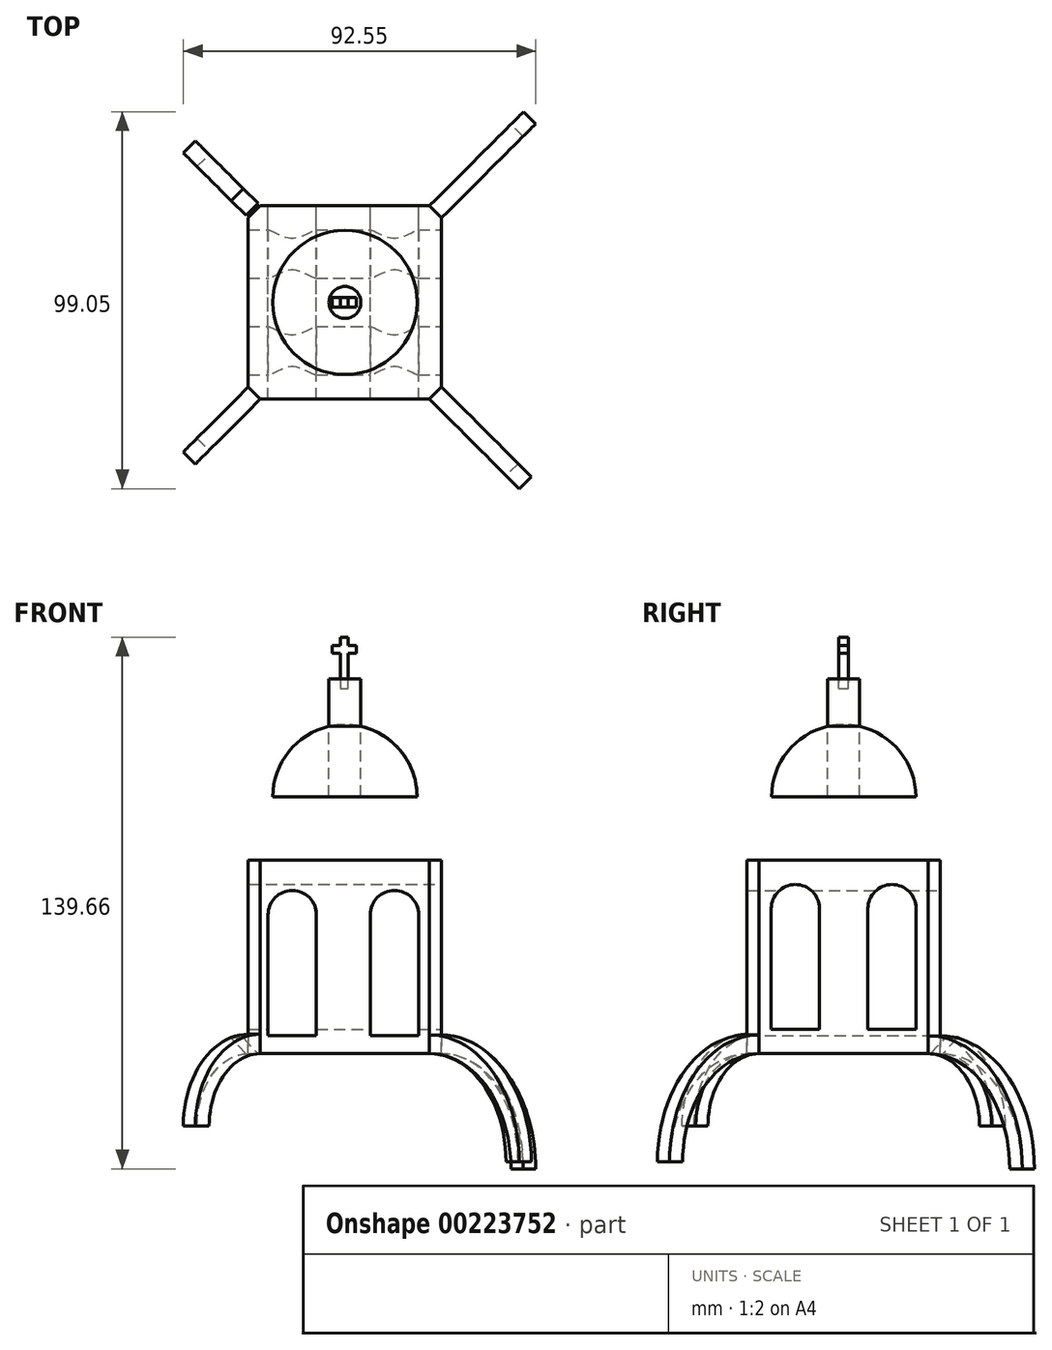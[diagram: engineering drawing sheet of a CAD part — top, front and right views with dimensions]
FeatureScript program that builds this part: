
annotation { "Feature Type Name" : "Feature", "Feature Type Description" : "" }
export const myFeature = defineFeature(function(context is Context, id is Id, definition is map)
    precondition{}
    {
        {
            var Q0;
            Q0=qCreatedBy(makeId("Front.planeOp"),FACE);
            var sketch = newSketch(context, id + "F0", { "sketchPlane" : qUnion([Q0])});
            skLineSegment(sketch, "E0.bottom", {"start": v(-25.4, -25.4) * mm, "end": v(25.4, -25.4) * mm});
            skLineSegment(sketch, "E0.top", {"start": v(-25.4, 25.4) * mm, "end": v(25.4, 25.4) * mm});
            skLineSegment(sketch, "E0.left", {"start": v(-25.4, -25.4) * mm, "end": v(-25.4, 25.4) * mm});
            skLineSegment(sketch, "E0.right", {"start": v(25.4, -25.4) * mm, "end": v(25.4, 25.4) * mm});
            skPoint(sketch, "E0.middle", {"position": v(0, 0) * mm});
            skLineSegment(sketch, "E1.bottom", {"start": v(0, 25.4) * mm, "end": v(-18.94, 25.4) * mm});
            skLineSegment(sketch, "E1.top", {"start": v(0, 42.12) * mm, "end": v(-18.94, 42.12) * mm});
            skLineSegment(sketch, "E1.left", {"start": v(0, 25.4) * mm, "end": v(0, 42.12) * mm});
            skLineSegment(sketch, "E1.right", {"start": v(-18.94, 25.4) * mm, "end": v(-18.94, 42.12) * mm});
            skArc(sketch, "E2", {"start": v(-18.94, 42.12) * mm, "mid": v(-13.4, 55.52) * mm, "end": v(0, 61.07) * mm});
            skLineSegment(sketch, "E3", {"start": v(0, 61.07) * mm, "end": v(0, 25.4) * mm});
            skLineSegment(sketch, "E4.bottom", {"start": v(0, 25.4) * mm, "end": v(-4.2, 25.4) * mm});
            skLineSegment(sketch, "E4.top", {"start": v(0, 73.03) * mm, "end": v(-4.2, 73.03) * mm});
            skLineSegment(sketch, "E4.left", {"start": v(0, 25.4) * mm, "end": v(0, 73.03) * mm});
            skLineSegment(sketch, "E4.right", {"start": v(-4.2, 25.4) * mm, "end": v(-4.2, 73.03) * mm});
            skSolve(sketch);
        }
        {
            var Q0;
            Q0=makeQuery(id+"F0.imprint","IMPRINT",FACE,{"disambiguationData":[TD([[makeQuery(id+"F0.imprint","IMPRINT",EDGE,{"derivedFrom":sQuery(id+"F0.wireOp",EDGE,"E0.bottom")}),1.0]])]});
            var sketch = newSketch(context, id + "F1", { "sketchPlane" : qUnion([Q0])});
            skLineSegment(sketch, "E5.bottom", {"start": v(-7.5, -20.63) * mm, "end": v(-20.2, -20.63) * mm});
            skLineSegment(sketch, "E5.top", {"start": v(-7.5, 11.12) * mm, "end": v(-20.2, 11.12) * mm});
            skLineSegment(sketch, "E5.left", {"start": v(-7.5, -20.63) * mm, "end": v(-7.5, 11.12) * mm});
            skLineSegment(sketch, "E5.right", {"start": v(-20.2, -20.63) * mm, "end": v(-20.2, 11.12) * mm});
            skPoint(sketch, "E5.middle", {"position": v(-13.84, -4.76) * mm});
            skLineSegment(sketch, "E6.bottom", {"start": v(6.65, -20.63) * mm, "end": v(19.35, -20.63) * mm});
            skLineSegment(sketch, "E6.top", {"start": v(6.65, 11.12) * mm, "end": v(19.35, 11.12) * mm});
            skLineSegment(sketch, "E6.left", {"start": v(6.65, -20.63) * mm, "end": v(6.65, 11.12) * mm});
            skLineSegment(sketch, "E6.right", {"start": v(19.35, -20.63) * mm, "end": v(19.35, 11.12) * mm});
            skPoint(sketch, "E6.middle", {"position": v(13, -4.76) * mm});
            skPoint(sketch, "E6.middle.positionSnap0", {"position": v(-7.5, -4.76) * mm});
            skPoint(sketch, "E6.centerSnap0", {"position": v(-7.5, -4.76) * mm});
            skArc(sketch, "E7", {"start": v(-7.5, 11.12) * mm, "mid": v(-13.84, 17.47) * mm, "end": v(-20.2, 11.12) * mm});
            skArc(sketch, "E8", {"start": v(19.35, 11.12) * mm, "mid": v(13, 17.47) * mm, "end": v(6.65, 11.12) * mm});
            skSolve(sketch);
        }
        {
            var Q0;
            {var subQ0=sQuery(id+"F0.wireOp",EDGE,"E1.top");Q0=makeQuery(id+"F0.imprint","IMPRINT",FACE,{"disambiguationData":[TD([[makeQuery(id+"F0.imprint","IMPRINT",EDGE,{"derivedFrom":subQ0}),-1.0]])]});}
            var Q1;
            {var subQ0=sQuery(id+"F0.wireOp",EDGE,"E1.bottom");Q1=makeQuery(id+"F0.imprint","IMPRINT",FACE,{"disambiguationData":[TD([[makeQuery(id+"F0.imprint","IMPRINT",EDGE,{"derivedFrom":subQ0}),-1.0]])]});}
            var Q2;
            {var subQ5=sQuery(id+"F0.wireOp",EDGE,"E4.top");Q2=makeQuery(id+"F0.imprint","IMPRINT",FACE,{"disambiguationData":[TD([[makeQuery(id+"F0.imprint","IMPRINT",EDGE,{"derivedFrom":subQ5}),1.0]])]});}
            var Q3;
            Q3=sQuery(id+"F0.wireOp",EDGE,"E3");
            revolve(context, id + "F2", {"entities" : qUnion([Q0, Q1, Q2]), "axis" : qUnion([Q3]), "revolveType" : RevolveType.FULL});
        }
        {
            var Q0;
            Q0=makeQuery(id+"F1.imprint","IMPRINT",FACE,{"disambiguationData":[TD([[makeQuery(id+"F1.imprint","IMPRINT",EDGE,{"derivedFrom":sQuery(id+"F1.wireOp",EDGE,"E5.bottom")}),1.0]])]});
            extrude(context, id + "F3", {"entities" : qUnion([Q0]), "operationType" : NewBodyOperationType.ADD, "endBound" : BoundingType.SYMMETRIC, "depth" : 50.8 * mm});
        }
        {
            var Q0;
            Q0=makeQuery(id+"F3.opExtrude","SWEPT_FACE",FACE,{"disambiguationData":[OSD([sQuery(id+"F0.wireOp",EDGE,"E0.right")])]});
            var sketch = newSketch(context, id + "F4", { "sketchPlane" : qUnion([Q0])});
            skLineSegment(sketch, "E9.bottom", {"start": v(-19.05, -19.05) * mm, "end": v(-6.35, -19.05) * mm});
            skLineSegment(sketch, "E9.top", {"start": v(-19.05, 12.7) * mm, "end": v(-6.35, 12.7) * mm});
            skLineSegment(sketch, "E9.left", {"start": v(-19.05, -19.05) * mm, "end": v(-19.05, 12.7) * mm});
            skLineSegment(sketch, "E9.right", {"start": v(-6.35, -19.05) * mm, "end": v(-6.35, 12.7) * mm});
            skPoint(sketch, "E9.middle", {"position": v(-12.7, -3.18) * mm});
            skLineSegment(sketch, "E10.bottom", {"start": v(6.35, -19.05) * mm, "end": v(19.05, -19.05) * mm});
            skLineSegment(sketch, "E10.top", {"start": v(6.35, 12.7) * mm, "end": v(19.05, 12.7) * mm});
            skLineSegment(sketch, "E10.left", {"start": v(6.35, -19.05) * mm, "end": v(6.35, 12.7) * mm});
            skLineSegment(sketch, "E10.right", {"start": v(19.05, -19.05) * mm, "end": v(19.05, 12.7) * mm});
            skPoint(sketch, "E10.middle", {"position": v(12.7, -3.18) * mm});
            skPoint(sketch, "E10.middle.positionSnap0", {"position": v(-19.05, -3.18) * mm});
            skPoint(sketch, "E10.centerSnap0", {"position": v(-19.05, -3.18) * mm});
            skArc(sketch, "E11", {"start": v(-6.35, 12.7) * mm, "mid": v(-12.7, 19.05) * mm, "end": v(-19.05, 12.7) * mm});
            skArc(sketch, "E12", {"start": v(19.05, 12.7) * mm, "mid": v(12.7, 19.05) * mm, "end": v(6.35, 12.7) * mm});
            skSolve(sketch);
        }
        {
            var Q0;
            Q0 = qSketchRegion(id + "F4", true);
            extrude(context, id + "F5", {"entities" : qUnion([Q0]), "operationType" : NewBodyOperationType.REMOVE, "oppositeDirection" : true, "depth" : 50.8 * mm});
        }
        {
            var Q0;
            Q0=qCreatedBy(makeId("Front.planeOp"),FACE);
            var sketch = newSketch(context, id + "F6", { "sketchPlane" : qUnion([Q0])});
            skLineSegment(sketch, "E13", {"start": v(0.86, 70.49) * mm, "end": v(0.86, 79.78) * mm});
            skLineSegment(sketch, "E14", {"start": v(0.86, 79.78) * mm, "end": v(2.97, 79.78) * mm});
            skLineSegment(sketch, "E15", {"start": v(2.97, 79.78) * mm, "end": v(2.97, 81.89) * mm});
            skLineSegment(sketch, "E16", {"start": v(2.97, 81.89) * mm, "end": v(0.86, 81.89) * mm});
            skLineSegment(sketch, "E17", {"start": v(0.86, 81.89) * mm, "end": v(0.86, 84) * mm});
            skLineSegment(sketch, "E18", {"start": v(0.86, 84) * mm, "end": v(-1.25, 84) * mm});
            skLineSegment(sketch, "E19", {"start": v(-1.25, 84) * mm, "end": v(-1.25, 81.89) * mm});
            skLineSegment(sketch, "E20", {"start": v(-1.25, 81.89) * mm, "end": v(-3.36, 81.89) * mm});
            skLineSegment(sketch, "E21", {"start": v(-3.36, 81.89) * mm, "end": v(-3.36, 79.78) * mm});
            skLineSegment(sketch, "E22", {"start": v(-3.36, 79.78) * mm, "end": v(-1.25, 79.78) * mm});
            skLineSegment(sketch, "E23", {"start": v(-1.25, 79.78) * mm, "end": v(-1.25, 70.47) * mm});
            skLineSegment(sketch, "E24", {"start": v(-1.25, 70.47) * mm, "end": v(0.86, 70.49) * mm});
            skSolve(sketch);
        }
        {
            var Q0;
            Q0 = qSketchRegion(id + "F6", true);
            extrude(context, id + "F7", {"entities" : qUnion([Q0]), "endBound" : BoundingType.SYMMETRIC, "depth" : 2.54 * mm});
        }
        {
            var Q0;
            Q0=makeQuery(id+"F3.opExtrude","CAP_EDGE",EDGE,{"disambiguationData":[OSD([sQuery(id+"F0.wireOp",EDGE,"E0.right")])],"isStart":false});
            var Q1;
            Q1=makeQuery(id+"F3.opExtrude","CAP_EDGE",EDGE,{"disambiguationData":[OSD([sQuery(id+"F0.wireOp",EDGE,"E0.left")])],"isStart":false});
            var Q2;
            Q2=makeQuery(id+"F3.opExtrude","CAP_EDGE",EDGE,{"disambiguationData":[OSD([sQuery(id+"F0.wireOp",EDGE,"E0.right")])],"isStart":true});
            var Q3;
            Q3=makeQuery(id+"F3.opExtrude","CAP_EDGE",EDGE,{"disambiguationData":[OSD([sQuery(id+"F0.wireOp",EDGE,"E0.left")])],"isStart":true});
            chamfer(context, id + "F8", {"entities" : qUnion([Q0, Q1, Q2, Q3]), "width" : 3.17 * mm, "tangentPropagation" : true});
        }
        {
            var Q0;
            {var subQ0=sQuery(id+"F0.wireOp",EDGE,"E0.left");Q0=makeQuery(id+"F8.opChamfer","BLEND_FACE",FACE,{"disambiguationData":[OSD([subQ0]),TDD([makeQuery(id+"F3.opExtrude","CAP_EDGE",EDGE,{"disambiguationData":[OSD([subQ0])],"isStart":false})])]});}
            var sketch = newSketch(context, id + "F9", { "sketchPlane" : qUnion([Q0])});
            skLineSegment(sketch, "E25.bottom", {"start": v(-2.25, -25.4) * mm, "end": v(2.25, -25.4) * mm});
            skLineSegment(sketch, "E25.top", {"start": v(-2.25, -20.32) * mm, "end": v(2.25, -20.32) * mm});
            skLineSegment(sketch, "E25.left", {"start": v(-2.25, -25.4) * mm, "end": v(-2.25, -20.32) * mm});
            skLineSegment(sketch, "E25.right", {"start": v(2.25, -25.4) * mm, "end": v(2.25, -20.32) * mm});
            skLineSegment(sketch, "E26.top", {"start": v(-2.25, -44.45) * mm, "end": v(2.25, -44.45) * mm});
            skLineSegment(sketch, "E26.left", {"start": v(-2.25, -25.4) * mm, "end": v(-2.25, -44.45) * mm});
            skLineSegment(sketch, "E26.right", {"start": v(2.25, -25.4) * mm, "end": v(2.25, -44.45) * mm});
            skSolve(sketch);
        }
        {
            var Q0;
            Q0=makeQuery(id+"F9.imprint","IMPRINT",FACE,{"disambiguationData":[TD([[makeQuery(id+"F9.imprint","IMPRINT",EDGE,{"derivedFrom":sQuery(id+"F9.wireOp",EDGE,"E25.top")}),-1.0]])]});
            var Q1;
            Q1=sQuery(id+"F9.wireOp",EDGE,"E26.top");
            revolve(context, id + "F10", {"operationType" : NewBodyOperationType.ADD, "entities" : qUnion([Q0]), "axis" : qUnion([Q1]), "revolveType" : RevolveType.ONE_DIRECTION, "angle" : 90 * degree});
        }
        {
            var Q0;
            {var subQ0=sQuery(id+"F0.wireOp",EDGE,"E0.left");Q0=makeQuery(id+"F8.opChamfer","BLEND_FACE",FACE,{"disambiguationData":[OSD([subQ0]),TDD([makeQuery(id+"F3.opExtrude","CAP_EDGE",EDGE,{"disambiguationData":[OSD([subQ0])],"isStart":true})])]});}
            var sketch = newSketch(context, id + "F11", { "sketchPlane" : qUnion([Q0])});
            skLineSegment(sketch, "E27.bottom", {"start": v(-2.25, -25.4) * mm, "end": v(2.25, -25.4) * mm});
            skLineSegment(sketch, "E27.top", {"start": v(-2.25, -20.32) * mm, "end": v(2.25, -20.32) * mm});
            skLineSegment(sketch, "E27.left", {"start": v(-2.25, -25.4) * mm, "end": v(-2.25, -20.32) * mm});
            skLineSegment(sketch, "E27.right", {"start": v(2.25, -25.4) * mm, "end": v(2.25, -20.32) * mm});
            skLineSegment(sketch, "E28.bottom", {"start": v(-2.25, -25.4) * mm, "end": v(2.22, -25.4) * mm});
            skLineSegment(sketch, "E28.top", {"start": v(-2.25, -44.45) * mm, "end": v(2.22, -44.45) * mm});
            skLineSegment(sketch, "E28.left", {"start": v(-2.25, -25.4) * mm, "end": v(-2.25, -44.45) * mm});
            skLineSegment(sketch, "E28.right", {"start": v(2.22, -25.4) * mm, "end": v(2.22, -44.45) * mm});
            skSolve(sketch);
        }
        {
            var Q0;
            Q0=makeQuery(id+"F11.imprint","IMPRINT",FACE,{"disambiguationData":[TD([[makeQuery(id+"F11.imprint","IMPRINT",EDGE,{"derivedFrom":sQuery(id+"F11.wireOp",EDGE,"E27.bottom")}),-1.0]])]});
            var Q1;
            Q1=sQuery(id+"F11.wireOp",EDGE,"E28.top");
            revolve(context, id + "F12", {"entities" : qUnion([Q0]), "axis" : qUnion([Q1]), "revolveType" : RevolveType.ONE_DIRECTION, "angle" : 90 * degree});
        }
        {
            var Q0;
            {var subQ0=sQuery(id+"F0.wireOp",EDGE,"E0.right");Q0=makeQuery(id+"F8.opChamfer","BLEND_FACE",FACE,{"disambiguationData":[OSD([subQ0]),TDD([makeQuery(id+"F3.opExtrude","CAP_EDGE",EDGE,{"disambiguationData":[OSD([subQ0])],"isStart":false})])]});}
            var sketch = newSketch(context, id + "F13", { "sketchPlane" : qUnion([Q0])});
            skLineSegment(sketch, "E29.bottom", {"start": v(-2.25, -25.4) * mm, "end": v(2.25, -25.4) * mm});
            skLineSegment(sketch, "E29.top", {"start": v(-2.25, -20.5) * mm, "end": v(2.25, -20.5) * mm});
            skLineSegment(sketch, "E29.left", {"start": v(-2.25, -25.4) * mm, "end": v(-2.25, -20.5) * mm});
            skLineSegment(sketch, "E29.right", {"start": v(2.25, -25.4) * mm, "end": v(2.25, -20.5) * mm});
            skLineSegment(sketch, "E30.top", {"start": v(-2.25, -53.82) * mm, "end": v(2.25, -53.82) * mm});
            skLineSegment(sketch, "E30.left", {"start": v(-2.25, -25.4) * mm, "end": v(-2.25, -53.82) * mm});
            skLineSegment(sketch, "E30.right", {"start": v(2.25, -25.4) * mm, "end": v(2.25, -53.82) * mm});
            skSolve(sketch);
        }
        {
            var Q0;
            {var subQ0=sQuery(id+"F0.wireOp",EDGE,"E0.right");Q0=makeQuery(id+"F8.opChamfer","BLEND_FACE",FACE,{"disambiguationData":[OSD([subQ0]),TDD([makeQuery(id+"F3.opExtrude","CAP_EDGE",EDGE,{"disambiguationData":[OSD([subQ0])],"isStart":true})])]});}
            var sketch = newSketch(context, id + "F14", { "sketchPlane" : qUnion([Q0])});
            skLineSegment(sketch, "E31.bottom", {"start": v(-2.25, -25.4) * mm, "end": v(2.25, -25.4) * mm});
            skLineSegment(sketch, "E31.top", {"start": v(-2.25, -20.75) * mm, "end": v(2.25, -20.75) * mm});
            skLineSegment(sketch, "E31.left", {"start": v(-2.25, -25.4) * mm, "end": v(-2.25, -20.75) * mm});
            skLineSegment(sketch, "E31.right", {"start": v(2.25, -25.4) * mm, "end": v(2.25, -20.75) * mm});
            skLineSegment(sketch, "E32.bottom", {"start": v(-2.25, -25.4) * mm, "end": v(2.22, -25.4) * mm});
            skPoint(sketch, "E33.oppositeSnap0", {"position": v(0, -25.4) * mm});
            skLineSegment(sketch, "E34.bottom", {"start": v(-2.25, -25.4) * mm, "end": v(2.29, -25.4) * mm});
            skLineSegment(sketch, "E34.top", {"start": v(-2.25, -55.66) * mm, "end": v(2.29, -55.66) * mm});
            skLineSegment(sketch, "E34.left", {"start": v(-2.25, -25.4) * mm, "end": v(-2.25, -55.66) * mm});
            skLineSegment(sketch, "E34.right", {"start": v(2.29, -25.4) * mm, "end": v(2.29, -55.66) * mm});
            skSolve(sketch);
        }
        {
            var Q0;
            Q0=makeQuery(id+"F13.imprint","IMPRINT",FACE,{"disambiguationData":[TD([[makeQuery(id+"F13.imprint","IMPRINT",EDGE,{"derivedFrom":sQuery(id+"F13.wireOp",EDGE,"E29.top")}),-1.0]])]});
            var Q1;
            Q1=sQuery(id+"F13.wireOp",EDGE,"E30.top");
            revolve(context, id + "F15", {"operationType" : NewBodyOperationType.ADD, "entities" : qUnion([Q0]), "axis" : qUnion([Q1]), "revolveType" : RevolveType.ONE_DIRECTION, "angle" : 90 * degree});
        }
        {
            var Q0;
            Q0=makeQuery(id+"F14.imprint","IMPRINT",FACE,{"disambiguationData":[TD([[makeQuery(id+"F14.imprint","IMPRINT",EDGE,{"derivedFrom":sQuery(id+"F14.wireOp",EDGE,"E31.top")}),-1.0]])]});
            var Q1;
            Q1=sQuery(id+"F14.wireOp",EDGE,"E34.top");
            var Q2;
            Q2=sQuery(id+"F14.wireOp",EDGE,"E34.top");
            revolve(context, id + "F16", {"operationType" : NewBodyOperationType.ADD, "entities" : qUnion([Q0]), "surfaceEntities" : qUnion([Q1]), "axis" : qUnion([Q2]), "revolveType" : RevolveType.ONE_DIRECTION, "angle" : 90 * degree});
        }
        {
            var Q0;
            Q0=makeQuery(id+"F15.opRevolve","CAP_EDGE",EDGE,{"disambiguationData":[OSD([sQuery(id+"F13.wireOp",EDGE,"E29.top")])],"isStart":true});
            var Q1;
            Q1=makeQuery(id+"F10.opRevolve","CAP_EDGE",EDGE,{"disambiguationData":[OSD([sQuery(id+"F9.wireOp",EDGE,"E25.top")])],"isStart":true});
            var Q2;
            Q2=makeQuery(id+"F12.opRevolve","CAP_EDGE",EDGE,{"disambiguationData":[OSD([sQuery(id+"F11.wireOp",EDGE,"E27.top")])],"isStart":true});
            var Q3;
            Q3=makeQuery(id+"F16.opRevolve","CAP_EDGE",EDGE,{"disambiguationData":[OSD([sQuery(id+"F14.wireOp",EDGE,"E31.top")])],"isStart":true});
            chamfer(context, id + "F17", {"entities" : qUnion([Q0, Q1, Q2, Q3]), "width" : 5.08 * mm, "tangentPropagation" : true});
        }
    });
